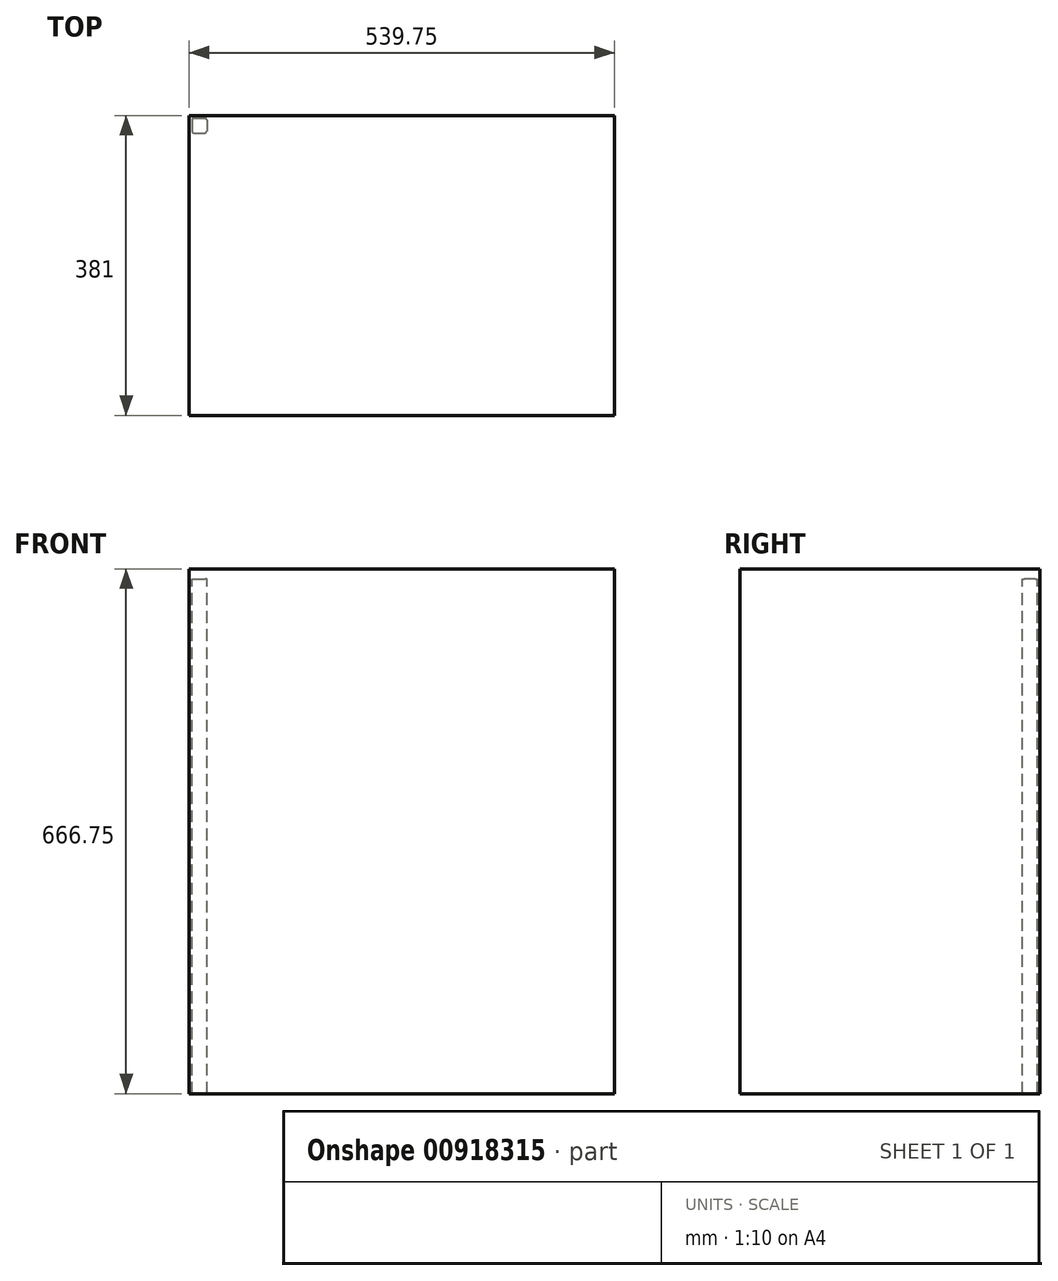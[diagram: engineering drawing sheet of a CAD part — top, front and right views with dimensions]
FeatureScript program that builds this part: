
annotation { "Feature Type Name" : "Feature", "Feature Type Description" : "" }
export const myFeature = defineFeature(function(context is Context, id is Id, definition is map)
    precondition{}
    {
        {
            var Q0;
            Q0=qCreatedBy(makeId("Right.planeOp"),FACE);
            var sketch = newSketch(context, id + "F0", { "sketchPlane" : qUnion([Q0])});
            skLineSegment(sketch, "E0", {"start": v(0, 0) * mm, "end": v(0, 628.65) * mm, "construction": true});
            skLineSegment(sketch, "E1", {"start": v(0, 628.65) * mm, "end": v(190.5, 628.65) * mm, "construction": true});
            skLineSegment(sketch, "E2.bottom", {"start": v(190.5, 628.65) * mm, "end": v(-190.5, 628.65) * mm});
            skLineSegment(sketch, "E2.top", {"start": v(190.5, 641.35) * mm, "end": v(-190.5, 641.35) * mm});
            skLineSegment(sketch, "E2.left", {"start": v(190.5, 628.65) * mm, "end": v(190.5, 641.35) * mm});
            skLineSegment(sketch, "E2.right", {"start": v(-190.5, 628.65) * mm, "end": v(-190.5, 641.35) * mm});
            skSolve(sketch);
        }
        {
            var Q0;
            Q0=makeQuery(id+"F0.imprint","IMPRINT",FACE,{"disambiguationData":[TD([[makeQuery(id+"F0.imprint","IMPRINT",EDGE,{"derivedFrom":sQuery(id+"F0.wireOp",EDGE,"E2.bottom")}),-1.0]])]});
            extrude(context, id + "F1", {"entities" : qUnion([Q0]), "depth" : 539.75 * mm, "offsetDistance" : 25.4 * mm});
        }
        {
            var Q0;
            Q0=makeQuery(id+"F1.opExtrude","SWEPT_FACE",FACE,{"disambiguationData":[OSD([sQuery(id+"F0.wireOp",EDGE,"E2.bottom")])]});
            var sketch = newSketch(context, id + "F2", { "sketchPlane" : qUnion([Q0])});
            skLineSegment(sketch, "E3", {"start": v(0, 190.5) * mm, "end": v(25.4, 190.5) * mm, "construction": true});
            skLineSegment(sketch, "E4.bottom", {"start": v(5.72, 187.32) * mm, "end": v(19.68, 187.32) * mm});
            skLineSegment(sketch, "E4.top", {"start": v(5.72, 168.27) * mm, "end": v(19.68, 168.27) * mm});
            skLineSegment(sketch, "E4.left", {"start": v(3.17, 184.78) * mm, "end": v(3.17, 170.81) * mm});
            skLineSegment(sketch, "E4.right", {"start": v(22.22, 184.78) * mm, "end": v(22.22, 170.81) * mm});
            skPoint(sketch, "E4.middle", {"position": v(12.7, 177.8) * mm});
            skPoint(sketch, "E5.visualSharp", {"position": v(3.17, 187.32) * mm});
            skArc(sketch, "E5.filletArc", {"start": v(5.72, 187.32) * mm, "mid": v(3.92, 186.58) * mm, "end": v(3.17, 184.78) * mm});
            skPoint(sketch, "E6.visualSharp", {"position": v(22.22, 187.32) * mm});
            skArc(sketch, "E6.filletArc", {"start": v(22.23, 184.78) * mm, "mid": v(21.48, 186.58) * mm, "end": v(19.68, 187.32) * mm});
            skPoint(sketch, "E7.visualSharp", {"position": v(22.22, 168.27) * mm});
            skArc(sketch, "E7.filletArc", {"start": v(19.68, 168.27) * mm, "mid": v(21.48, 169.02) * mm, "end": v(22.23, 170.81) * mm});
            skPoint(sketch, "E8.visualSharp", {"position": v(3.17, 168.27) * mm});
            skArc(sketch, "E8.filletArc", {"start": v(3.17, 170.81) * mm, "mid": v(3.92, 169.02) * mm, "end": v(5.72, 168.27) * mm});
            skLineSegment(sketch, "E9", {"start": v(12.7, 177.8) * mm, "end": v(12.7, 190.5) * mm, "construction": true});
            skLineSegment(sketch, "E10", {"start": v(0, 190.5) * mm, "end": v(0, 165.1) * mm});
            skPoint(sketch, "E11.endSnap0", {"position": v(0, 177.8) * mm});
            skLineSegment(sketch, "E12", {"start": v(12.7, 177.8) * mm, "end": v(0, 177.8) * mm, "construction": true});
            skLineSegment(sketch, "E13", {"start": v(0, 0) * mm, "end": v(539.75, 0) * mm, "construction": true});
            skArc(sketch, "E14.MirrorCS", {"start": v(22.22, -184.78) * mm, "mid": v(21.48, -186.58) * mm, "end": v(19.68, -187.32) * mm});
            skArc(sketch, "E15.MirrorCS", {"start": v(3.17, -170.81) * mm, "mid": v(3.92, -169.02) * mm, "end": v(5.72, -168.27) * mm});
            skArc(sketch, "E16.MirrorCS", {"start": v(19.68, -168.27) * mm, "mid": v(21.48, -169.02) * mm, "end": v(22.22, -170.81) * mm});
            skArc(sketch, "E17.MirrorCS", {"start": v(5.72, -187.32) * mm, "mid": v(3.92, -186.58) * mm, "end": v(3.17, -184.78) * mm});
            skLineSegment(sketch, "E18.MirrorCS", {"start": v(12.7, -177.8) * mm, "end": v(12.7, -190.5) * mm, "construction": true});
            skLineSegment(sketch, "E19.MirrorCS", {"start": v(0, -190.5) * mm, "end": v(0, -165.1) * mm});
            skLineSegment(sketch, "E20.MirrorCS", {"start": v(5.72, -168.27) * mm, "end": v(19.68, -168.27) * mm});
            skLineSegment(sketch, "E21.MirrorCS", {"start": v(3.17, -184.78) * mm, "end": v(3.17, -170.81) * mm});
            skLineSegment(sketch, "E22.MirrorCS", {"start": v(5.72, -187.32) * mm, "end": v(19.68, -187.32) * mm});
            skPoint(sketch, "E23.MirrorP", {"position": v(22.22, -187.32) * mm});
            skPoint(sketch, "E24.MirrorP", {"position": v(12.7, -177.8) * mm});
            skPoint(sketch, "E25.MirrorP", {"position": v(0, -177.8) * mm});
            skLineSegment(sketch, "E26.MirrorCS", {"start": v(12.7, -177.8) * mm, "end": v(0, -177.8) * mm, "construction": true});
            skLineSegment(sketch, "E27.MirrorCS", {"start": v(22.22, -184.78) * mm, "end": v(22.22, -170.81) * mm});
            skPoint(sketch, "E28.MirrorP", {"position": v(22.22, -168.27) * mm});
            skPoint(sketch, "E29.MirrorP", {"position": v(3.17, -168.27) * mm});
            skPoint(sketch, "E30.MirrorP", {"position": v(3.17, -187.32) * mm});
            skLineSegment(sketch, "E31.MirrorCS", {"start": v(0, -190.5) * mm, "end": v(25.4, -190.5) * mm, "construction": true});
            skSolve(sketch);
        }
        {
            var Q0;
            Q0=makeQuery(id+"F2.imprint","IMPRINT",FACE,{"disambiguationData":[TD([[makeQuery(id+"F2.imprint","IMPRINT",EDGE,{"derivedFrom":sQuery(id+"F2.wireOp",EDGE,"E4.bottom")}),-1.0]])]});
            var Q1;
            Q1=makeQuery(id+"F2.imprint","IMPRINT",FACE,{"disambiguationData":[TD([[makeQuery(id+"F2.imprint","IMPRINT",EDGE,{"derivedFrom":sQuery(id+"F2.wireOp",EDGE,"E14.MirrorCS")}),-1.0]])]});
            extrude(context, id + "F3", {"entities" : qUnion([Q0, Q1]), "operationType" : NewBodyOperationType.ADD, "depth" : 654.05 * mm, "offsetDistance" : 25.4 * mm});
        }
    });
